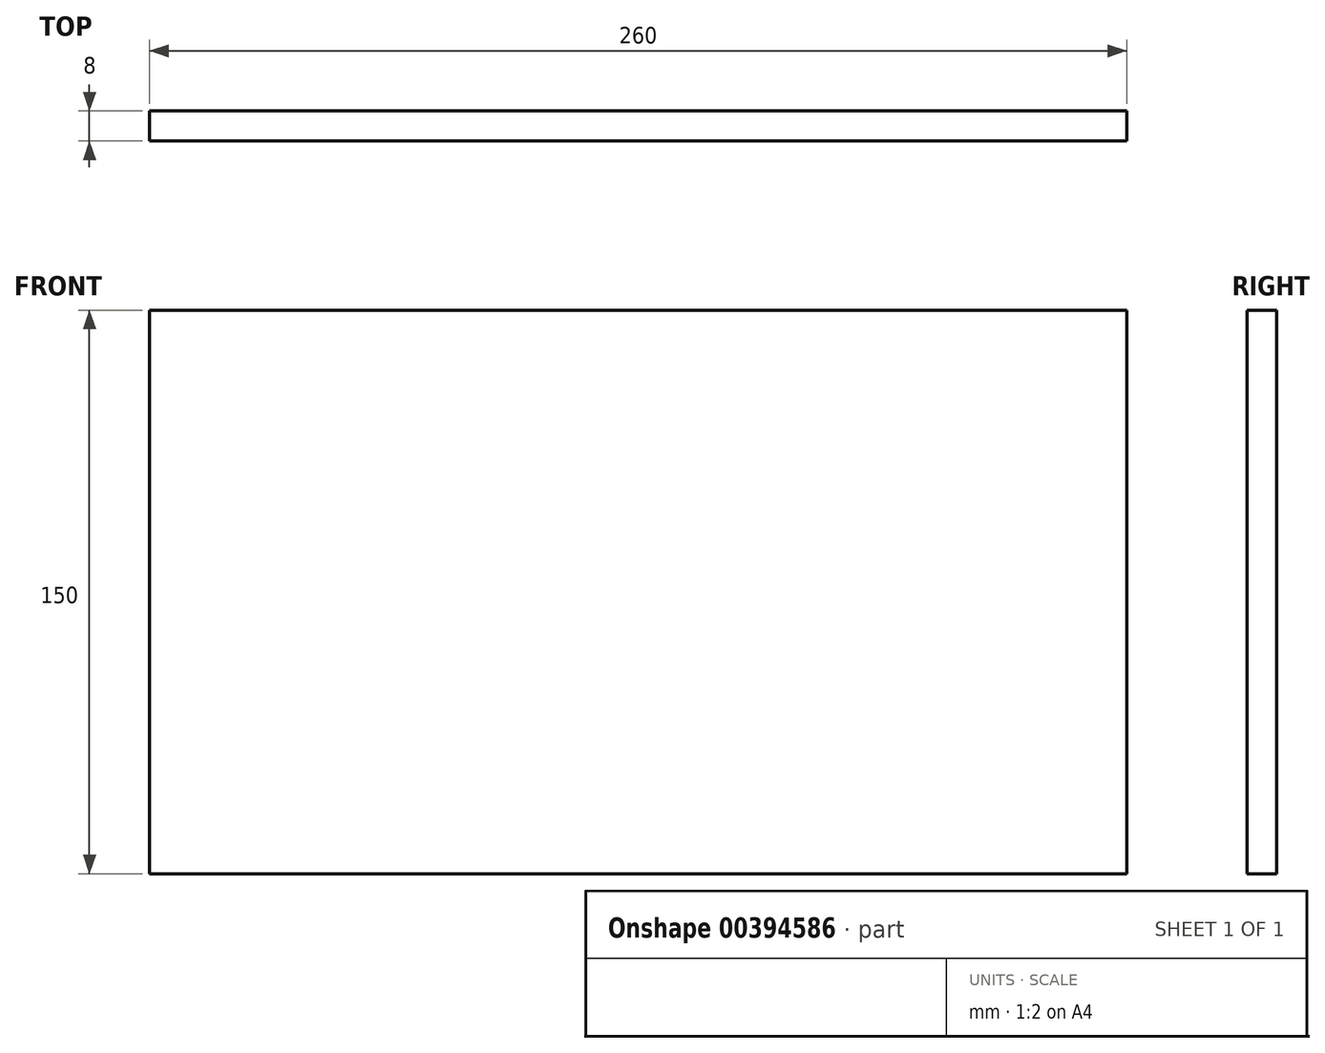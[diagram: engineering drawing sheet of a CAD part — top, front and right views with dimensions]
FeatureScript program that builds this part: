
annotation { "Feature Type Name" : "Feature", "Feature Type Description" : "" }
export const myFeature = defineFeature(function(context is Context, id is Id, definition is map)
    precondition{}
    {
        {
            var Q0;
            Q0=qCreatedBy(makeId("Front.planeOp"),FACE);
            var sketch = newSketch(context, id + "F0", { "sketchPlane" : qUnion([Q0])});
            skLineSegment(sketch, "E0.bottom", {"start": v(130, -75) * mm, "end": v(-130, -75) * mm});
            skLineSegment(sketch, "E0.top", {"start": v(130, 75) * mm, "end": v(-130, 75) * mm});
            skLineSegment(sketch, "E0.left", {"start": v(130, -75) * mm, "end": v(130, 75) * mm});
            skLineSegment(sketch, "E0.right", {"start": v(-130, -75) * mm, "end": v(-130, 75) * mm});
            skPoint(sketch, "E0.middle", {"position": v(0, 0) * mm});
            skSolve(sketch);
        }
        {
            var Q0;
            Q0=makeQuery(id+"F0.imprint","IMPRINT",FACE,{"disambiguationData":[TD([[makeQuery(id+"F0.imprint","IMPRINT",EDGE,{"derivedFrom":sQuery(id+"F0.wireOp",EDGE,"E0.bottom")}),-1.0]])]});
            extrude(context, id + "F1", {"entities" : qUnion([Q0]), "depth" : 8 * mm});
        }
    });
